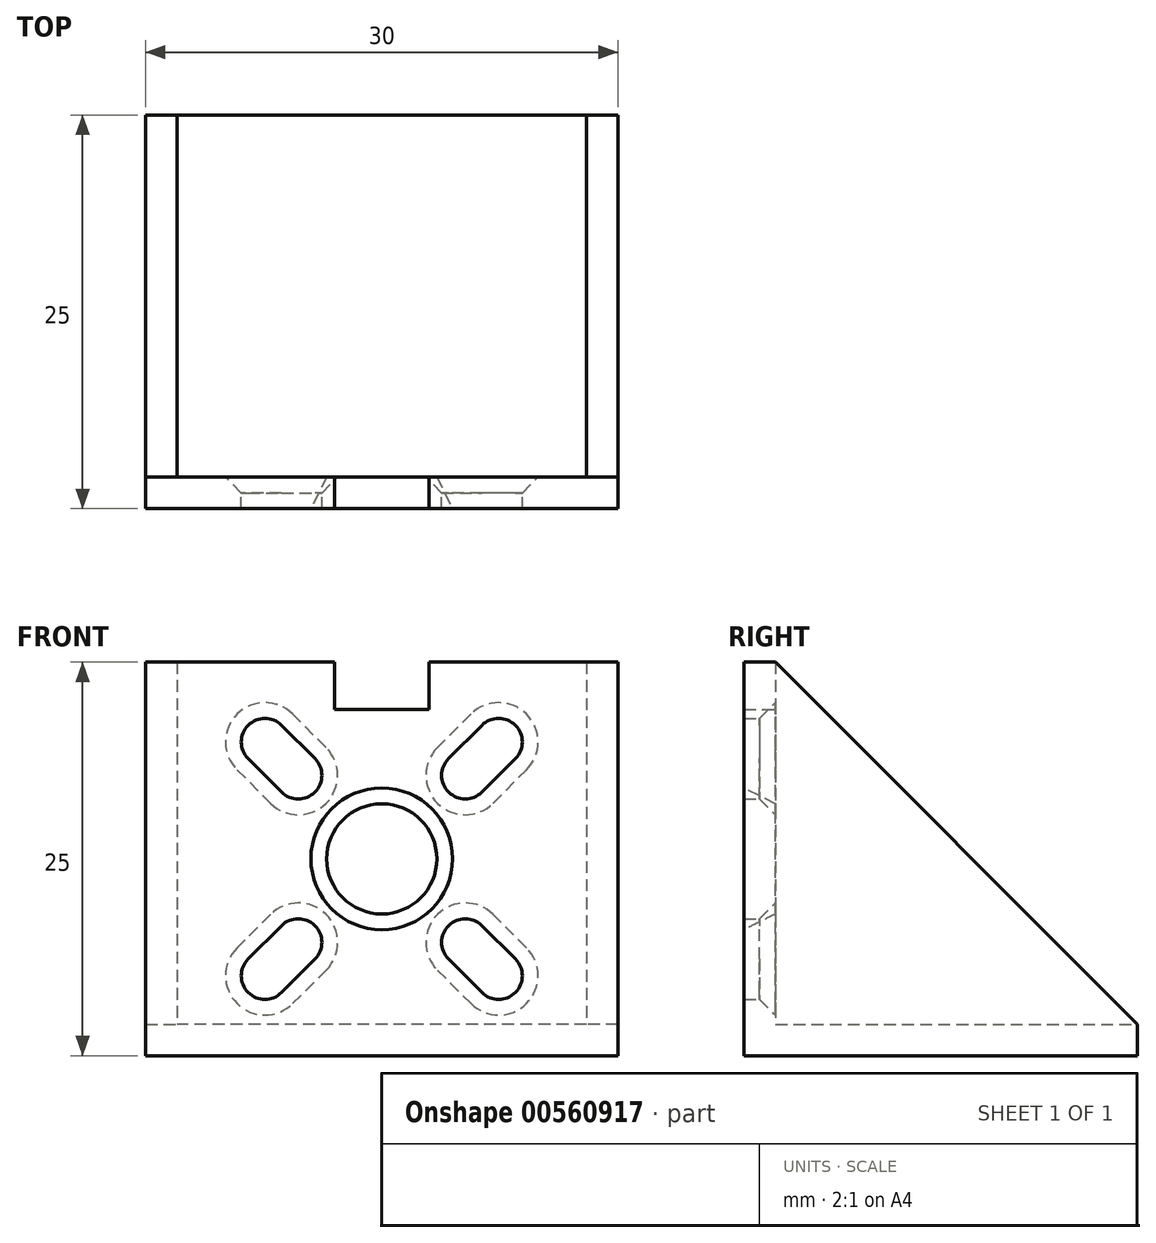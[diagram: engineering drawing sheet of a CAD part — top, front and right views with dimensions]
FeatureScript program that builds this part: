
annotation { "Feature Type Name" : "Feature", "Feature Type Description" : "" }
export const myFeature = defineFeature(function(context is Context, id is Id, definition is map)
    precondition{}
    {
        {
            var Q0;
            Q0=qCreatedBy(makeId("Front.planeOp"),FACE);
            var sketch = newSketch(context, id + "F0", { "sketchPlane" : qUnion([Q0])});
            skLineSegment(sketch, "E0.bottom", {"start": v(-15, 12.5) * mm, "end": v(15, 12.5) * mm});
            skLineSegment(sketch, "E0.top", {"start": v(-15, -12.5) * mm, "end": v(15, -12.5) * mm});
            skLineSegment(sketch, "E0.left", {"start": v(-15, 12.5) * mm, "end": v(-15, -12.5) * mm});
            skLineSegment(sketch, "E0.right", {"start": v(15, 12.5) * mm, "end": v(15, -12.5) * mm});
            skCircle(sketch, "E1", {"center": v(0, 0) * mm, "radius": 3.5 * mm});
            skLineSegment(sketch, "E2", {"start": v(19.53, 19.53) * mm, "end": v(-23.58, -23.58) * mm, "construction": true});
            skLineSegment(sketch, "E3", {"start": v(-21.08, 21.08) * mm, "end": v(27.03, -27.03) * mm, "construction": true});
            skCircle(sketch, "E4", {"center": v(-7.42, 7.42) * mm, "radius": 1.5 * mm});
            skCircle(sketch, "E5", {"center": v(-5.3, 5.3) * mm, "radius": 1.5 * mm});
            skLineSegment(sketch, "E6", {"start": v(-6.36, 8.49) * mm, "end": v(-4.24, 6.36) * mm});
            skLineSegment(sketch, "E7", {"start": v(-8.49, 6.36) * mm, "end": v(-6.36, 4.24) * mm});
            skCircle(sketch, "E8.1.0", {"center": v(-7.42, -7.42) * mm, "radius": 1.5 * mm});
            skLineSegment(sketch, "E8.1.1", {"start": v(-8.49, -6.36) * mm, "end": v(-6.36, -4.24) * mm});
            skLineSegment(sketch, "E8.1.2", {"start": v(-6.36, -8.49) * mm, "end": v(-4.24, -6.36) * mm});
            skCircle(sketch, "E8.1.3", {"center": v(-5.3, -5.3) * mm, "radius": 1.5 * mm});
            skCircle(sketch, "E8.2.0", {"center": v(7.42, -7.42) * mm, "radius": 1.5 * mm});
            skLineSegment(sketch, "E8.2.1", {"start": v(6.36, -8.49) * mm, "end": v(4.24, -6.36) * mm});
            skLineSegment(sketch, "E8.2.2", {"start": v(8.49, -6.36) * mm, "end": v(6.36, -4.24) * mm});
            skCircle(sketch, "E8.2.3", {"center": v(5.3, -5.3) * mm, "radius": 1.5 * mm});
            skCircle(sketch, "E8.3.0", {"center": v(7.42, 7.42) * mm, "radius": 1.5 * mm});
            skLineSegment(sketch, "E8.3.1", {"start": v(8.49, 6.36) * mm, "end": v(6.36, 4.24) * mm});
            skLineSegment(sketch, "E8.3.2", {"start": v(6.36, 8.49) * mm, "end": v(4.24, 6.36) * mm});
            skCircle(sketch, "E8.3.3", {"center": v(5.3, 5.3) * mm, "radius": 1.5 * mm});
            skLineSegment(sketch, "E9.bottom", {"start": v(-3, 12.5) * mm, "end": v(3, 12.5) * mm});
            skLineSegment(sketch, "E9.top", {"start": v(-3, 9.5) * mm, "end": v(3, 9.5) * mm});
            skLineSegment(sketch, "E9.left", {"start": v(-3, 12.5) * mm, "end": v(-3, 9.5) * mm});
            skLineSegment(sketch, "E9.right", {"start": v(3, 12.5) * mm, "end": v(3, 9.5) * mm});
            skSolve(sketch);
        }
        {
            var Q0;
            Q0=makeQuery(id+"F0.imprint","IMPRINT",FACE,{"disambiguationData":[TD([[makeQuery(id+"F0.imprint","IMPRINT",EDGE,{"derivedFrom":sQuery(id+"F0.wireOp",EDGE,"E0.bottom")}),-1.0]])]});
            extrude(context, id + "F1", {"entities" : qUnion([Q0]), "depth" : 2 * mm, "offsetDistance" : 25 * mm});
        }
        {
            var Q0;
            Q0=qCreatedBy(makeId("Right.planeOp"),FACE);
            var sketch = newSketch(context, id + "F2", { "sketchPlane" : qUnion([Q0])});
            skLineSegment(sketch, "E10.bottom", {"start": v(0, -12.5) * mm, "end": v(23, -12.5) * mm});
            skLineSegment(sketch, "E10.top", {"start": v(0, -10.5) * mm, "end": v(23, -10.5) * mm});
            skLineSegment(sketch, "E10.left", {"start": v(0, -12.5) * mm, "end": v(0, -10.5) * mm});
            skLineSegment(sketch, "E10.right", {"start": v(23, -12.5) * mm, "end": v(23, -10.5) * mm});
            skLineSegment(sketch, "E11", {"start": v(23, -10.5) * mm, "end": v(0, 12.5) * mm});
            skLineSegment(sketch, "E12", {"start": v(0, 12.5) * mm, "end": v(0, -10.5) * mm});
            skSolve(sketch);
        }
        {
            var Q0;
            Q0=makeQuery(id+"F2.imprint","IMPRINT",FACE,{"disambiguationData":[TD([[makeQuery(id+"F2.imprint","IMPRINT",EDGE,{"derivedFrom":sQuery(id+"F2.wireOp",EDGE,"E10.bottom")}),1.0]])]});
            extrude(context, id + "F3", {"entities" : qUnion([Q0]), "operationType" : NewBodyOperationType.ADD, "depth" : 30 * mm, "offsetDistance" : 25 * mm, "symmetric" : true});
        }
        {
            var Q0;
            Q0=makeQuery(id+"F2.imprint","IMPRINT",FACE,{"disambiguationData":[TD([[makeQuery(id+"F2.imprint","IMPRINT",EDGE,{"derivedFrom":sQuery(id+"F2.wireOp",EDGE,"E10.top")}),1.0]])]});
            extrude(context, id + "F4", {"entities" : qUnion([Q0]), "operationType" : NewBodyOperationType.ADD, "depth" : 15 * mm, "offsetDistance" : 25 * mm, "hasSecondDirection" : true, "secondDirectionOppositeDirection" : false, "secondDirectionDepth" : 13 * mm});
        }
        {
            var Q0;
            Q0=makeQuery(id+"F2.imprint","IMPRINT",FACE,{"disambiguationData":[TD([[makeQuery(id+"F2.imprint","IMPRINT",EDGE,{"derivedFrom":sQuery(id+"F2.wireOp",EDGE,"E10.top")}),1.0]])]});
            extrude(context, id + "F5", {"entities" : qUnion([Q0]), "operationType" : NewBodyOperationType.ADD, "oppositeDirection" : true, "depth" : 15 * mm, "offsetDistance" : 25 * mm, "hasSecondDirection" : true, "secondDirectionOppositeDirection" : true, "secondDirectionDepth" : 13 * mm});
        }
        {
            var Q0;
            Q0=makeQuery(id+"F1.opExtrude","CAP_EDGE",EDGE,{"disambiguationData":[OSD([sQuery(id+"F0.wireOp",EDGE,"E8.3.2")])],"isStart":true});
            var Q1;
            Q1=makeQuery(id+"F1.opExtrude","CAP_EDGE",EDGE,{"disambiguationData":[OSD([sQuery(id+"F0.wireOp",EDGE,"E6")])],"isStart":true});
            var Q2;
            Q2=makeQuery(id+"F1.opExtrude","CAP_EDGE",EDGE,{"disambiguationData":[OSD([sQuery(id+"F0.wireOp",EDGE,"E8.1.1")])],"isStart":true});
            var Q3;
            Q3=makeQuery(id+"F1.opExtrude","CAP_EDGE",EDGE,{"disambiguationData":[OSD([sQuery(id+"F0.wireOp",EDGE,"E8.2.2")])],"isStart":true});
            chamfer(context, id + "F6", {"entities" : qUnion([Q0, Q1, Q2, Q3]), "width" : 1 * mm, "tangentPropagation" : true});
        }
        {
            var Q0;
            Q0=makeQuery(id+"F1.opExtrude","CAP_EDGE",EDGE,{"disambiguationData":[OSD([sQuery(id+"F0.wireOp",EDGE,"E1")])],"isStart":false});
            chamfer(context, id + "F7", {"entities" : qUnion([Q0]), "chamferType" : ChamferType.TWO_OFFSETS, "width1" : 2 * mm, "oppositeDirection" : false, "width2" : 1 * mm, "tangentPropagation" : true});
        }
    });
